# Revit family: FC-110-38-3.5
name_source: partatom
category: Aparatos sanitarios
units: mm (PartAtom-declared; Revit-internal decimal feet)

## family parameters
Compartido = Sí
Corte con vacíos al cargar = No
Cota de conector redondo = Diámetro de uso
Número OmniClass = 23.45.00.00
Punto de cálculo de habitación = No
Se basa en plano de trabajo = No
Siempre vertical = Sí
Tipo de pieza = Normal
Título OmniClass = Sanitary, Laundry, and Cleaning Equipment

## types (2) — shared parameters
Chrome = Brass Chromed
Comentarios de tipo = Flushvalves
Compliance = NOM-005-CONAGUA-1996
Conexión AF = Sí
Connection = 1" Feeding Connection
Detection Range = 0 - 15.74"
Elevación por defecto = 0"
Fabricante = Helvex
Features = Operates With a 6 Vcc Power Supply; Manual Flush Button; Antibacterial Coating Manual Flush Button; Left or Right Connection
Feeding Voltage = 6 V
Max. Working Pressure = 85.3 psi
Note = Feeding Pipe Must Be 1 ¼" and Connection a 1 ¼" - 1" Reductor to Stop Valve
Outlet Lenght Hose = 59"
Power Consumption = 2 W

## per-type parameters (varying)
| type | Certification | Descripción | Documentation | Flow | Imagen de tipo | Min. Working Pressure | URL |
| FC-110-WC-4.8 | http://www.helvex.com.mx | 1.26 gpf, 32 or 38 AC Operated Electronic WC Flushvalve With Button | http://www.helvex.com.mx | 1.3 - 1.6 Gallons Per Flush | <Ninguno> | 14.2 psi | http://www.helvex.com.mx |
| FC-110-38-3.5 | https://www.helvex.com.mx | Electronic Flushometer Current Sensor for W. C. | https://www.helvex.com.mx | 0.92 Gallons Per Flush | FC-110-38-3.5.jpg | 28.4 psi | https://www.helvex.com.mx |

note: column(s) folded — value = type name in every type: Modelo

## geometry (parser evidence)
native form markers: Sweep x3
no freeform markers — native parametric forms only
